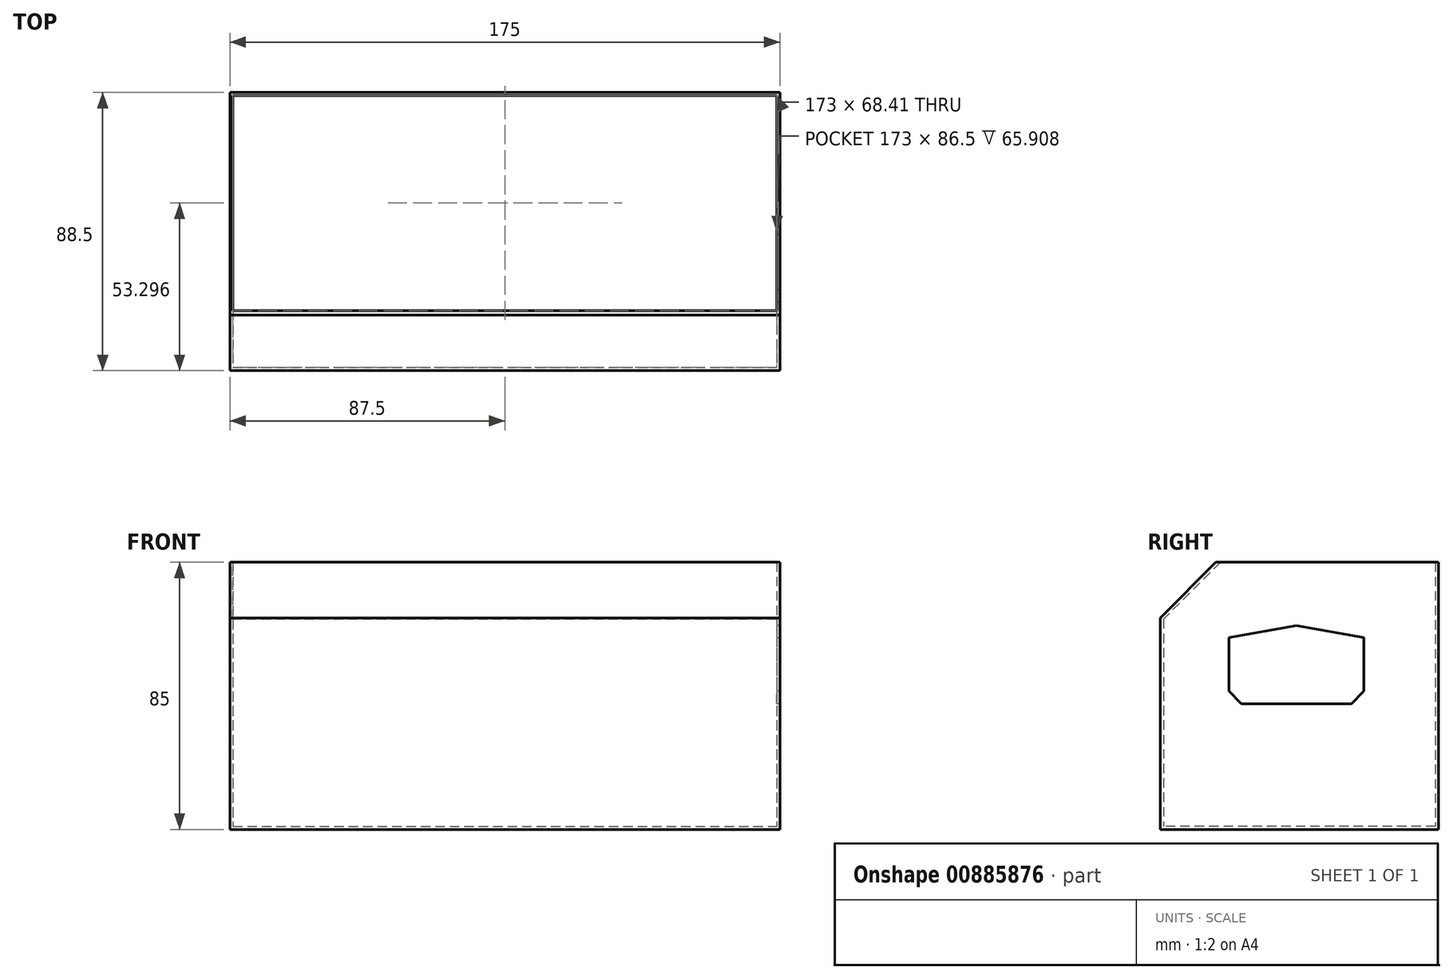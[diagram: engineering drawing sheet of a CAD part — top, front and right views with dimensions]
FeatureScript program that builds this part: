
annotation { "Feature Type Name" : "Feature", "Feature Type Description" : "" }
export const myFeature = defineFeature(function(context is Context, id is Id, definition is map)
    precondition{}
    {
        {
            var Q0;
            Q0=qCreatedBy(makeId("Top.planeOp"),FACE);
            var sketch = newSketch(context, id + "F0", { "sketchPlane" : qUnion([Q0])});
            skLineSegment(sketch, "E0.bottom", {"start": v(0, 0) * mm, "end": v(175, 0) * mm});
            skLineSegment(sketch, "E0.top", {"start": v(0, -88.5) * mm, "end": v(175, -88.5) * mm});
            skLineSegment(sketch, "E0.left", {"start": v(0, 0) * mm, "end": v(0, -88.5) * mm});
            skLineSegment(sketch, "E0.right", {"start": v(175, 0) * mm, "end": v(175, -88.5) * mm});
            skSolve(sketch);
        }
        {
            var Q0;
            Q0=qSketchRegion(id+"F0",true);
            extrude(context, id + "F1", {"entities" : qUnion([Q0]), "depth" : 85 * mm, "offsetDistance" : 25 * mm});
        }
        {
            var Q0;
            Q0=makeQuery(id+"F1.opExtrude","CAP_EDGE",EDGE,{"disambiguationData":[OSD([sQuery(id+"F0.wireOp",EDGE,"E0.top")])],"isStart":false});
            chamfer(context, id + "F2", {"entities" : qUnion([Q0]), "width" : 17.68 * mm, "tangentPropagation" : true});
        }
        {
            var Q0;
            Q0=makeQuery(id+"F1.opExtrude","CAP_FACE",FACE,{"disambiguationData":[OSD([sQuery(id+"F0.wireOp",EDGE,"E0.bottom"),sQuery(id+"F0.wireOp",EDGE,"E0.top"),sQuery(id+"F0.wireOp",EDGE,"E0.left"),sQuery(id+"F0.wireOp",EDGE,"E0.right")])],"isStart":false});
            shell(context, id + "F3", {"entities" : qUnion([Q0]), "thickness" : 1 * mm});
        }
        {
            var Q0;
            Q0=makeQuery(id+"F1.opExtrude","SWEPT_FACE",FACE,{"disambiguationData":[OSD([sQuery(id+"F0.wireOp",EDGE,"E0.right")])]});
            var sketch = newSketch(context, id + "F4", { "sketchPlane" : qUnion([Q0])});
            skLineSegment(sketch, "E1.bottom", {"start": v(-66.75, 65) * mm, "end": v(-23.75, 65) * mm});
            skLineSegment(sketch, "E1.top", {"start": v(-66.75, 40) * mm, "end": v(-23.75, 40) * mm});
            skLineSegment(sketch, "E1.left", {"start": v(-66.75, 65) * mm, "end": v(-66.75, 40) * mm});
            skLineSegment(sketch, "E1.right", {"start": v(-23.75, 65) * mm, "end": v(-23.75, 40) * mm});
            skSolve(sketch);
        }
        {
            var Q0;
            Q0=qSketchRegion(id+"F4",true);
            extrude(context, id + "F5", {"entities" : qUnion([Q0]), "operationType" : NewBodyOperationType.REMOVE, "oppositeDirection" : true, "depth" : 2 * mm, "offsetDistance" : 25 * mm});
        }
        {
            var Q0;
            Q0=makeQuery(id+"F5.boolean.opBoolean","COPY",EDGE,{"derivedFrom":makeQuery(id+"F5.opExtrude","SWEPT_EDGE",EDGE,{"disambiguationData":[OSD([sQuery(id+"F4.wireOp",EDGE,"E1.bottom"),sQuery(id+"F4.wireOp",EDGE,"E1.left")])]})});
            var Q1;
            Q1=makeQuery(id+"F5.boolean.opBoolean","COPY",EDGE,{"derivedFrom":makeQuery(id+"F5.opExtrude","SWEPT_EDGE",EDGE,{"disambiguationData":[OSD([sQuery(id+"F4.wireOp",EDGE,"E1.bottom"),sQuery(id+"F4.wireOp",EDGE,"E1.right")])]})});
            chamfer(context, id + "F6", {"entities" : qUnion([Q0, Q1]), "chamferType" : ChamferType.OFFSET_ANGLE, "width" : 4 * mm, "oppositeDirection" : false, "angle" : 80 * degree, "tangentPropagation" : true});
        }
        {
            var Q0;
            Q0=makeQuery(id+"F5.boolean.opBoolean","COPY",EDGE,{"derivedFrom":makeQuery(id+"F5.opExtrude","SWEPT_EDGE",EDGE,{"disambiguationData":[OSD([sQuery(id+"F4.wireOp",EDGE,"E1.top"),sQuery(id+"F4.wireOp",EDGE,"E1.left")])]})});
            var Q1;
            Q1=makeQuery(id+"F5.boolean.opBoolean","COPY",EDGE,{"derivedFrom":makeQuery(id+"F5.opExtrude","SWEPT_EDGE",EDGE,{"disambiguationData":[OSD([sQuery(id+"F4.wireOp",EDGE,"E1.top"),sQuery(id+"F4.wireOp",EDGE,"E1.right")])]})});
            chamfer(context, id + "F7", {"entities" : qUnion([Q0, Q1]), "width" : 4 * mm, "tangentPropagation" : true});
        }
    });
